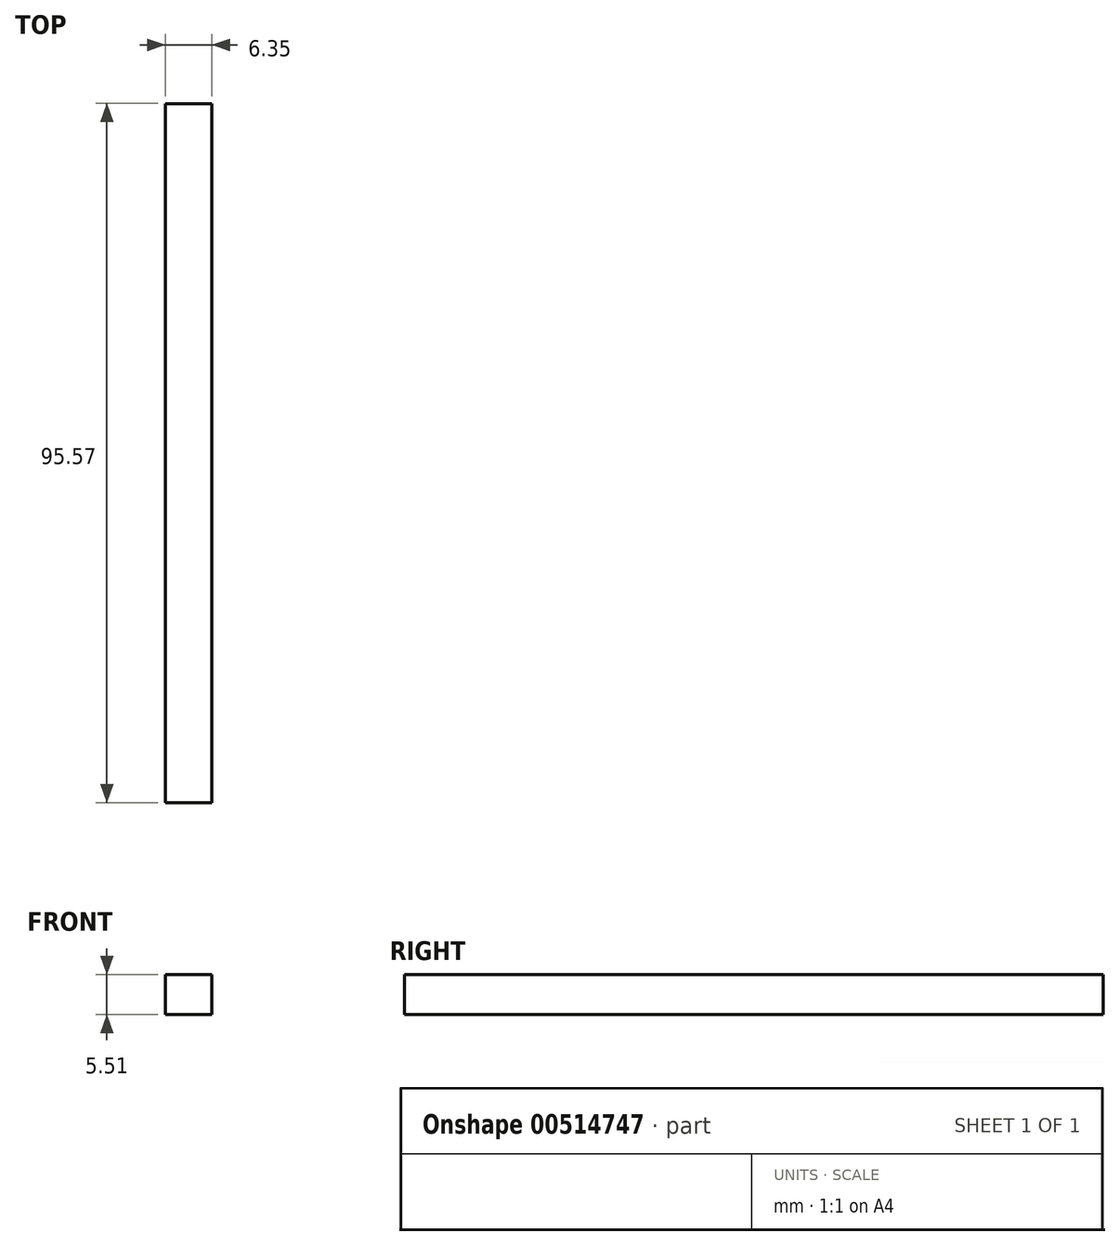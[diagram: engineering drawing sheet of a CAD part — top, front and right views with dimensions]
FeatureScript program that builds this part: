
annotation { "Feature Type Name" : "Feature", "Feature Type Description" : "" }
export const myFeature = defineFeature(function(context is Context, id is Id, definition is map)
    precondition{}
    {
        {
            var Q0;
            Q0=qCreatedBy(makeId("Right.planeOp"),FACE);
            var sketch = newSketch(context, id + "F0", { "sketchPlane" : qUnion([Q0])});
            skLineSegment(sketch, "E0.bottom", {"start": v(-43.86, 0) * mm, "end": v(51.7, 0) * mm});
            skLineSegment(sketch, "E0.top", {"start": v(-43.86, 5.51) * mm, "end": v(51.7, 5.51) * mm});
            skLineSegment(sketch, "E0.left", {"start": v(-43.86, 0) * mm, "end": v(-43.86, 5.51) * mm});
            skLineSegment(sketch, "E0.right", {"start": v(51.7, 0) * mm, "end": v(51.7, 5.51) * mm});
            skSolve(sketch);
        }
        {
            var Q0;
            Q0 = qSketchRegion(id + "F0", true);
            extrude(context, id + "F1", {"entities" : qUnion([Q0]), "depth" : 6.35 * mm, "offsetDistance" : 25.4 * mm});
        }
    });
